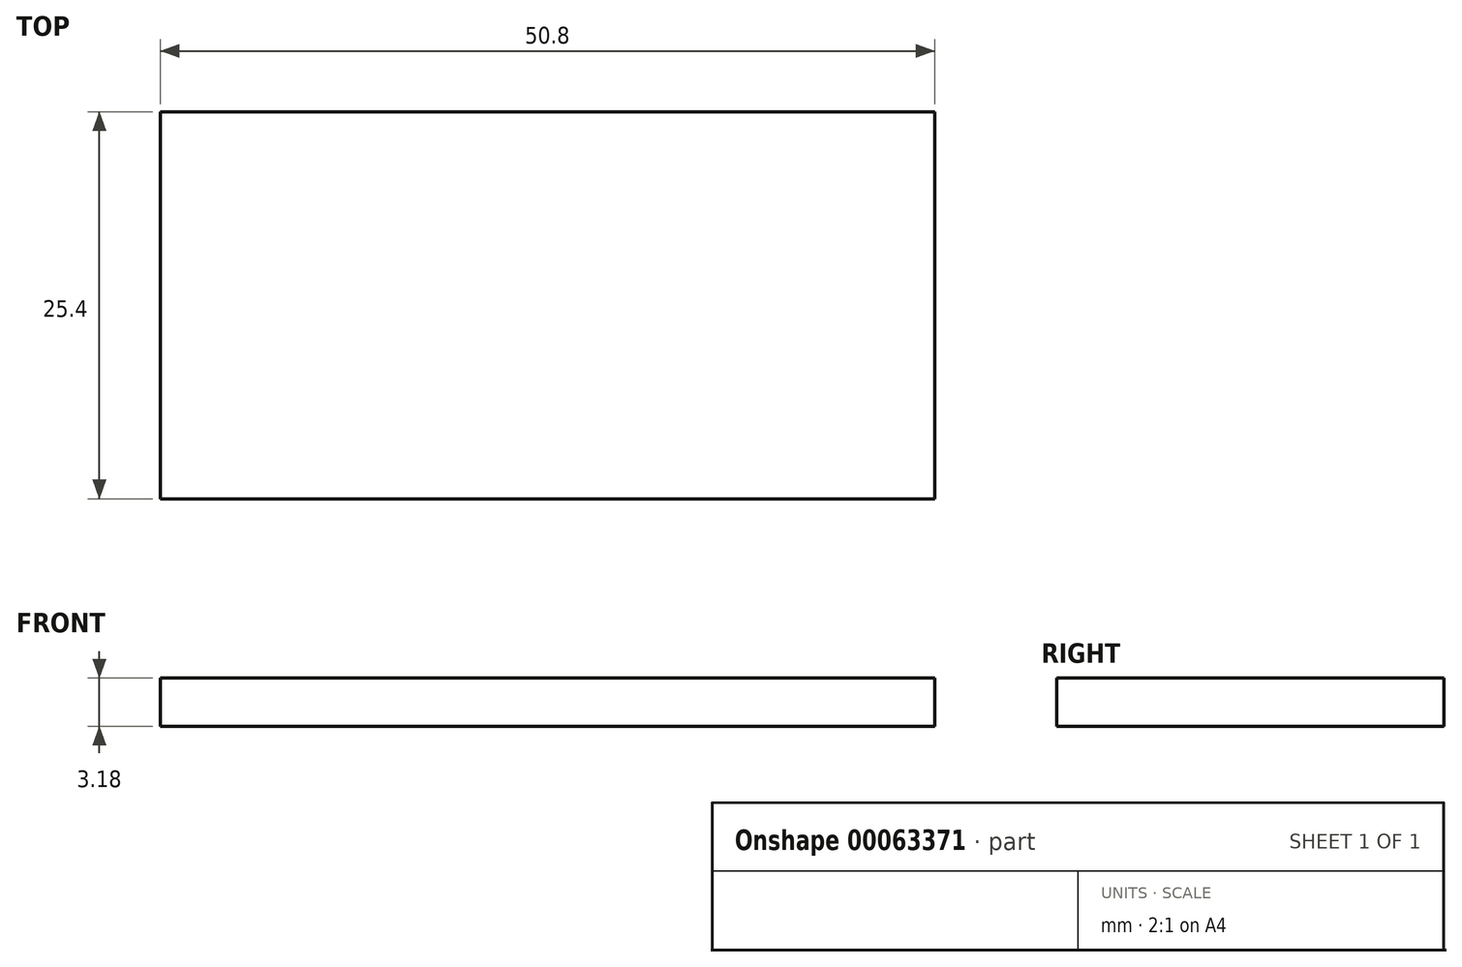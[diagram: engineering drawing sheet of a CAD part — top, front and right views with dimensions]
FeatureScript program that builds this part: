
annotation { "Feature Type Name" : "Feature", "Feature Type Description" : "" }
export const myFeature = defineFeature(function(context is Context, id is Id, definition is map)
    precondition{}
    {
        {
            var Q0;
            Q0=qCreatedBy(makeId("Top.planeOp"),FACE);
            var sketch = newSketch(context, id + "F0", { "sketchPlane" : qUnion([Q0])});
            skLineSegment(sketch, "E0.rect.bottom", {"start": v(25.4, 12.7) * mm, "end": v(-25.4, 12.7) * mm});
            skLineSegment(sketch, "E0.rect.top", {"start": v(25.4, -12.7) * mm, "end": v(-25.4, -12.7) * mm});
            skLineSegment(sketch, "E0.rect.left", {"start": v(25.4, 12.7) * mm, "end": v(25.4, -12.7) * mm});
            skLineSegment(sketch, "E0.rect.right", {"start": v(-25.4, 12.7) * mm, "end": v(-25.4, -12.7) * mm});
            skPoint(sketch, "E0.rect.middle", {"position": v(0, 0) * mm});
            skSolve(sketch);
        }
        {
            var Q0;
            Q0 = qSketchRegion(id + "F0", true);
            extrude(context, id + "F1", {"entities" : qUnion([Q0]), "endBound" : BoundingType.SYMMETRIC, "depth" : 3.17 * mm});
        }
    });
